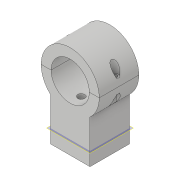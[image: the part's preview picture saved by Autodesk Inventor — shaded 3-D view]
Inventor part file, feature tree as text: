
AUTODESK INVENTOR PART (.ipt)
format: ipt  version: 2021 (Build 250183000, 183)  size: 210,432 bytes
history: native  units: mm
features: other x8, extrude x5, sketch x2, split x1, hole x1, imported_body x1
ambient origin geometry x8: Origin, YZ Plane, XZ Plane, XY Plane, X Axis, Y Axis, Z Axis, Center Point
bodies: Solid1 (feature_tree)
feature tree (18):
  extrude  "Extrusion1"  Depth=85.0mm
  other  "BoltPlane"
  other  "BoltHoles"
  extrude  "Extrusion2"  Depth=50.0mm
  extrude  "Extrusion3"  Depth=6.0mm
  other  "NutPlane"
  other  "NutHoles"
  extrude  "Extrusion4"  Depth=6.4mm
  other  "SplitPlane"
  split  "Split2"
  hole  "Hole2"  [1 undecoded]
  sketch  "Sketch4"  dims[d4=58.0mm d5=0.0mm d6=50.0mm d7=6.0mm d8=6.4mm d9=10.4mm d10=58.0mm d11=0.0mm d12=40.0mm d13=0.0mm d14=-80.0mm d15=10.4mm d16=70.0mm d17=0.0mm d18=0.0mm d28=12.5mm d29=6.2mm d30=6.0mm d31=4.0mm d32=2.0mm d33=90.0deg d34=8.0mm d35=0.0mm d36=10.2mm d37=10.2mm d38=18.0mm d39=62.0mm d40=0.0mm d41=94.0mm d42=-20.0mm d43=0.5mm d44=0.872665mm d45=0.5mm d46=0.872665mm]
  other  "BoltHeadLevel"
  other  "BoltHeadsPlane(35mm-M6-bolts)"
  extrude  "Extrusion5"  Depth=58.0mm TaperAngle=0.0deg
  sketch  "Sketch1"  dims[d0=55.9mm d1=85.0mm]
  other  "UPPER"
  imported_body  "BASE"
note: 1 required parameter value undecoded (feature->parameter linkage not recoverable at this tier; creation-order binding heuristic only, values carry confidence <= 0.55)
